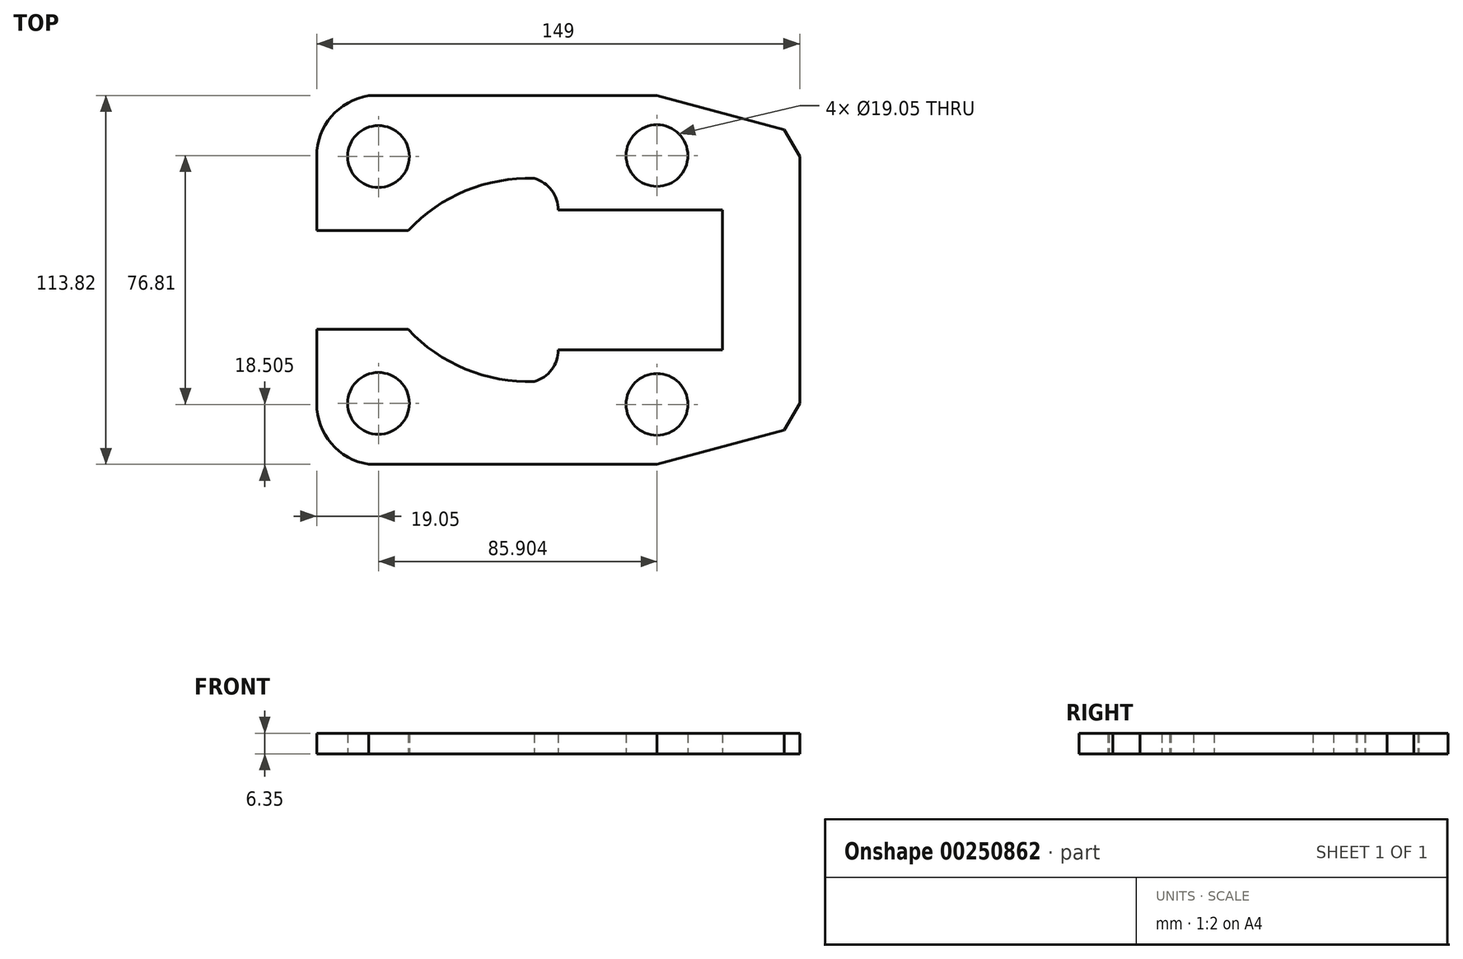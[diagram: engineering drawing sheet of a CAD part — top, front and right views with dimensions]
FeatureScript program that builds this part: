
annotation { "Feature Type Name" : "Feature", "Feature Type Description" : "" }
export const myFeature = defineFeature(function(context is Context, id is Id, definition is map)
    precondition{}
    {
        {
            var Q0;
            Q0=qCreatedBy(makeId("Top.planeOp"),FACE);
            var sketch = newSketch(context, id + "F0", { "sketchPlane" : qUnion([Q0])});
            skCircle(sketch, "E0", {"center": v(19.05, 38.1) * mm, "radius": 9.53 * mm});
            skArc(sketch, "E1", {"start": v(16.05, 56.91) * mm, "mid": v(4.56, 50.47) * mm, "end": v(0, 38.1) * mm});
            skLineSegment(sketch, "E2", {"start": v(0, 15.24) * mm, "end": v(28.19, 15.24) * mm});
            skLineSegment(sketch, "E3", {"start": v(16.05, 56.91) * mm, "end": v(104.95, 56.91) * mm});
            skLineSegment(sketch, "E4", {"start": v(0, 38.1) * mm, "end": v(0, 15.24) * mm});
            skCircle(sketch, "E5", {"center": v(104.95, 38.4) * mm, "radius": 9.53 * mm});
            skLineSegment(sketch, "E6", {"start": v(104.95, 56.91) * mm, "end": v(144.2, 46.4) * mm});
            skLineSegment(sketch, "E7", {"start": v(144.2, 46.4) * mm, "end": v(149, 38.1) * mm});
            skLineSegment(sketch, "E8", {"start": v(149, 38.1) * mm, "end": v(149, 0) * mm});
            skLineSegment(sketch, "E9", {"start": v(125.12, 21.57) * mm, "end": v(74.49, 21.57) * mm});
            skArc(sketch, "E10", {"start": v(74.49, 21.57) * mm, "mid": v(70.25, 29.82) * mm, "end": v(61.07, 31.19) * mm});
            skLineSegment(sketch, "E11.MirrorCS", {"start": v(0, -38.1) * mm, "end": v(0, -15.24) * mm});
            skLineSegment(sketch, "E12.MirrorCS", {"start": v(0, -15.24) * mm, "end": v(28.19, -15.24) * mm});
            skLineSegment(sketch, "E13.MirrorCS", {"start": v(125.12, -21.57) * mm, "end": v(74.49, -21.57) * mm});
            skLineSegment(sketch, "E14.MirrorCS", {"start": v(149, -38.1) * mm, "end": v(149, 0) * mm});
            skLineSegment(sketch, "E15.MirrorCS", {"start": v(144.2, -46.4) * mm, "end": v(149, -38.1) * mm});
            skLineSegment(sketch, "E16.MirrorCS", {"start": v(104.95, -56.91) * mm, "end": v(144.2, -46.4) * mm});
            skLineSegment(sketch, "E17.MirrorCS", {"start": v(16.05, -56.91) * mm, "end": v(104.95, -56.91) * mm});
            skArc(sketch, "E18.MirrorCS", {"start": v(16.05, -56.91) * mm, "mid": v(4.56, -50.47) * mm, "end": v(0, -38.1) * mm});
            skArc(sketch, "E19.MirrorC", {"start": v(74.49, -21.57) * mm, "mid": v(70.25, -29.82) * mm, "end": v(61.07, -31.19) * mm});
            skCircle(sketch, "E20.MirrorC", {"center": v(19.05, -38.1) * mm, "radius": 9.53 * mm});
            skCircle(sketch, "E21.MirrorC", {"center": v(104.95, -38.4) * mm, "radius": 9.53 * mm});
            skPoint(sketch, "E22.orphan", {"position": v(149, 21.57) * mm});
            skPoint(sketch, "E23.MirrorCS.end.orphan", {"position": v(125.12, -1.25) * mm});
            skPoint(sketch, "E23.MirrorCS.start.orphan", {"position": v(149, 0) * mm});
            skPoint(sketch, "E24.orphan", {"position": v(149, -21.57) * mm});
            skArc(sketch, "E25", {"start": v(67.13, 31.33) * mm, "mid": v(45.91, 27.51) * mm, "end": v(28.19, 15.24) * mm});
            skArc(sketch, "E26.MirrorCS", {"start": v(67.13, -31.33) * mm, "mid": v(45.91, -27.51) * mm, "end": v(28.19, -15.24) * mm});
            skPoint(sketch, "E27.orphan", {"position": v(56.38, 15.24) * mm});
            skPoint(sketch, "E28.orphan", {"position": v(56.38, -15.24) * mm});
            skPoint(sketch, "E29.orphan", {"position": v(0, 0) * mm});
            skPoint(sketch, "E30.start.orphan", {"position": v(125.12, 1.25) * mm});
            skLineSegment(sketch, "E31", {"start": v(125.12, -21.57) * mm, "end": v(125.12, 21.57) * mm});
            skSolve(sketch);
        }
        {
            var Q0;
            Q0 = qSketchRegion(id + "F0", true);
            extrude(context, id + "F1", {"entities" : qUnion([Q0]), "depth" : 6.35 * mm});
        }
    });
